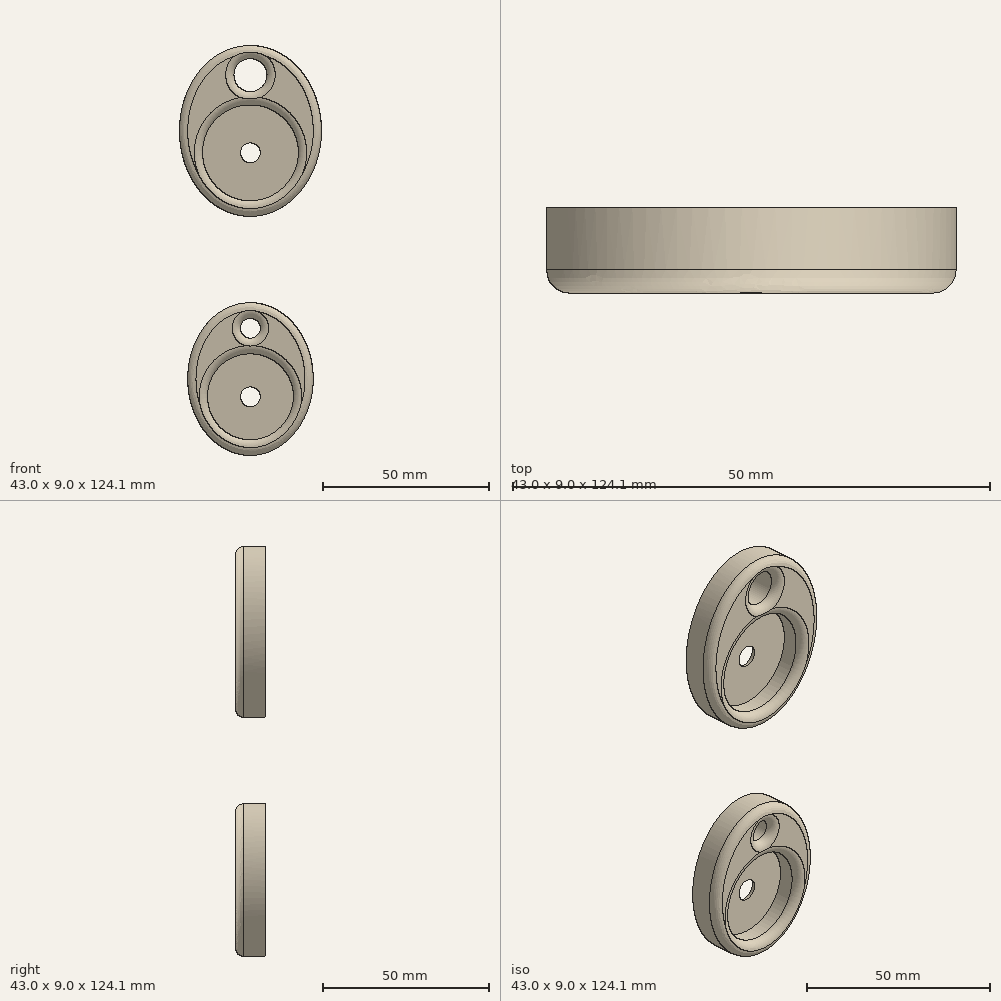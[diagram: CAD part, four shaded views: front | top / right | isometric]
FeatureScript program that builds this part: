
annotation { "Feature Type Name" : "Feature", "Feature Type Description" : "" }
export const myFeature = defineFeature(function(context is Context, id is Id, definition is map)
    precondition{}
    {
        {
            var Q0;
            Q0=qCreatedBy(makeId("Front.planeOp"),FACE);
            var sketch = newSketch(context, id + "F0", { "sketchPlane" : qUnion([Q0])});
            skCircle(sketch, "E0", {"center": v(0, 0) * mm, "radius": 13 * mm});
            skCircle(sketch, "E1", {"center": v(0, 0) * mm, "radius": 28.5 * mm});
            skLineSegment(sketch, "E2", {"start": v(0, 28.5) * mm, "end": v(0, 13) * mm, "construction": true});
            skPoint(sketch, "E3.middle", {"position": v(0, 20.75) * mm});
            skCircle(sketch, "E4", {"center": v(0, 20.75) * mm, "radius": 3 * mm});
            skCircle(sketch, "E5", {"center": v(0, 73.83) * mm, "radius": 14.5 * mm});
            skCircle(sketch, "E6", {"center": v(0, 73.83) * mm, "radius": 32.5 * mm});
            skLineSegment(sketch, "E7", {"start": v(0, 106.33) * mm, "end": v(0, 88.33) * mm, "construction": true});
            skCircle(sketch, "E8", {"center": v(0, 97.33) * mm, "radius": 5 * mm});
            skCircle(sketch, "E9", {"center": v(0, 97.33) * mm, "radius": 9 * mm});
            skLineSegment(sketch, "E10", {"start": v(0, 106.33) * mm, "end": v(0, 54.58) * mm, "construction": true});
            skEllipse(sketch, "E11", {"center": v(0, 80.46) * mm, "majorRadius": 25.88 * mm, "minorRadius": 21.5 * mm, "majorAxis": v(0, -1)});
            skCircle(sketch, "E12", {"center": v(0, 20.75) * mm, "radius": 7.75 * mm});
            skLineSegment(sketch, "E13", {"start": v(0, 28.5) * mm, "end": v(0, -17.75) * mm, "construction": true});
            skEllipse(sketch, "E14", {"center": v(0, 5.38) * mm, "majorRadius": 23.12 * mm, "minorRadius": 19 * mm, "majorAxis": v(0, -1)});
            skCircle(sketch, "E15", {"center": v(0, 73.83) * mm, "radius": 3 * mm});
            skCircle(sketch, "E16", {"center": v(0, 0) * mm, "radius": 3 * mm});
            skSolve(sketch);
        }
        {
            var Q0;
            {var subQ0=sQuery(id+"F0.wireOp",EDGE,"E5");Q0=makeQuery(id+"F0.imprint","IMPRINT",FACE,{"disambiguationData":[TD([[makeQuery(id+"F0.imprint","IMPRINT",EDGE,{"derivedFrom":subQ0}),-1.0]])]});}
            var Q1;
            Q1=makeQuery(id+"F0.imprint","IMPRINT",FACE,{"disambiguationData":[TD([[makeQuery(id+"F0.imprint","IMPRINT",EDGE,{"derivedFrom":sQuery(id+"F0.wireOp",EDGE,"E8")}),-1.0]])]});
            var Q2;
            {var subQ0=sQuery(id+"F0.wireOp",EDGE,"E0");Q2=makeQuery(id+"F0.imprint","IMPRINT",FACE,{"disambiguationData":[TD([[makeQuery(id+"F0.imprint","IMPRINT",EDGE,{"derivedFrom":subQ0}),-1.0]])]});}
            var Q3;
            Q3=makeQuery(id+"F0.imprint","IMPRINT",FACE,{"disambiguationData":[TD([[makeQuery(id+"F0.imprint","IMPRINT",EDGE,{"derivedFrom":sQuery(id+"F0.wireOp",EDGE,"E4")}),-1.0]])]});
            extrude(context, id + "F1", {"entities" : qUnion([Q0, Q1, Q2, Q3]), "depth" : 9 * mm, "offsetDistance" : 25 * mm});
        }
        {
            var Q0;
            Q0=makeQuery(id+"F0.imprint","IMPRINT",FACE,{"disambiguationData":[TD([[makeQuery(id+"F0.imprint","IMPRINT",EDGE,{"derivedFrom":sQuery(id+"F0.wireOp",EDGE,"E5")}),1.0]])]});
            var Q1;
            Q1=makeQuery(id+"F0.imprint","IMPRINT",FACE,{"disambiguationData":[TD([[makeQuery(id+"F0.imprint","IMPRINT",EDGE,{"derivedFrom":sQuery(id+"F0.wireOp",EDGE,"E0")}),1.0]])]});
            extrude(context, id + "F2", {"entities" : qUnion([Q0, Q1]), "operationType" : NewBodyOperationType.ADD, "depth" : 2 * mm, "offsetDistance" : 25 * mm});
        }
        {
            var Q0;
            Q0=makeQuery(id+"F1.opExtrude","CAP_EDGE",EDGE,{"disambiguationData":[OSD([sQuery(id+"F0.wireOp",EDGE,"E5")])],"isStart":false});
            var Q1;
            Q1=makeQuery(id+"F1.opExtrude","CAP_EDGE",EDGE,{"disambiguationData":[OSD([sQuery(id+"F0.wireOp",EDGE,"E0")])],"isStart":false});
            var Q2;
            Q2=makeQuery(id+"F1.opExtrude","CAP_EDGE",EDGE,{"disambiguationData":[OSD([sQuery(id+"F0.wireOp",EDGE,"E4")])],"isStart":false});
            var Q3;
            Q3=makeQuery(id+"F1.opExtrude","CAP_EDGE",EDGE,{"disambiguationData":[OSD([sQuery(id+"F0.wireOp",EDGE,"E8")])],"isStart":false});
            var Q4;
            Q4=makeQuery(id+"F1.opExtrude","CAP_EDGE",EDGE,{"disambiguationData":[OSD([sQuery(id+"F0.wireOp",EDGE,"E11")])],"isStart":false});
            var Q5;
            Q5=makeQuery(id+"F1.opExtrude","CAP_EDGE",EDGE,{"disambiguationData":[OSD([sQuery(id+"F0.wireOp",EDGE,"E14")])],"isStart":false});
            fillet(context, id + "F3", {"entities" : qUnion([Q0, Q1, Q2, Q3, Q4, Q5]), "radius" : 2.5 * mm, "tangentPropagation" : true, "allowEdgeOverflow" : false});
        }
        {
            var Q0;
            Q0=makeQuery(id+"F2.opExtrude","CAP_EDGE",EDGE,{"disambiguationData":[OSD([sQuery(id+"F0.wireOp",EDGE,"E15")])],"isStart":true});
            var Q1;
            Q1=makeQuery(id+"F2.opExtrude","CAP_EDGE",EDGE,{"disambiguationData":[OSD([sQuery(id+"F0.wireOp",EDGE,"E16")])],"isStart":true});
            fillet(context, id + "F4", {"entities" : qUnion([Q0, Q1]), "radius" : 2 * mm, "tangentPropagation" : true, "allowEdgeOverflow" : false});
        }
    });
